SOLIDWORKS PART (.sldprt)
format: sldprt  version: not decoded by parser v0  size: 498,176 bytes
history: native  units: mm
features: extrude x59, sketch x1 (+10 scaffold rows collapsed)
feature tree (70):
  scaffold x10  (default folders/planes/origin — collapsed)
  sketch  "Sketch1"  dims[c1.D1=~12.733394mm c1.D2=~15.484547mm c2.D1=22.86mm c2.D2=2.54mm c2.D4=2.54mm c2.D5=12.7mm c2.D6=2.54mm c2.D7=2.54mm c2.D8=2.54mm c2.D9=2.54mm c2.D10=2.54mm c2.D11=2.54mm c2.D13=10.3124mm c2.D14=~8.032185mm c2.D15=12.7mm c3.D9=2.54mm c3.D19=2.54mm c3.D4=2.54mm c3.D11=2.54mm c3.D18=2.54mm c4.D19=2.54mm c4.D7=~12.249777mm c4.D9=2.54mm c4.D18=2.54mm c5.D9=2.54mm c5.D16=2.54mm c5.D1=19.05mm c5.D2=~75.656875mm c6.D1=~12.696978mm c6.D2=~98.64952mm c7.D1=19.05mm c7.D2=3.175mm c7.D3=10.16mm c8.D2=~9.284402mm c8.D4=~112.960223mm c9.D2=9.525mm c9.D4=~113.490586mm c10.D4=~2.011859deg c11.D4=19.05mm c11.D2=~30.49108deg c12.D2=~13.842804mm c13.D2=~41.841832deg c14.D2=~12.93566mm c14.D12=101.6mm c14.D15=76.2mm c14.D16=~117.088215mm c14.D17=~111.932015mm c15.D16=~117.088215mm c15.D17=9.525mm c16.D16=9.525mm c16.D17=~72.799364mm c16.D15=76.2mm c17.D16=~107.263361mm c17.D17=103.251mm c17.D18=~89.259557mm c18.D18=~179.994237deg c19.D18=16.51mm c19.D19=~12.700868mm c19.D20=12.7mm c19.D21=12.7mm c19.D22=~12.94911mm c19.D23=~7.595379mm c19.D6=7.62mm c19.D10=12.7mm c19.D4=5.08mm c19.D7=15.24mm c19.D8=8.89mm c19.D9=~12.031811mm c20.D9=~30.579227deg c21.D9=~99.101888mm c22.D9=~38.079333deg c23.D9=~12.173949mm]
  extrude  "Extrude6"  Depth=6.35mm RestraintType=0
  extrude  "cosFMVItemName"  [1 undecoded]
  extrude  "cosLBCSymbolColor"  [1 undecoded]
  extrude  "cosRestraintRefPlaneName"  [1 undecoded]
  extrude  "cosFMVItemName"  [1 undecoded]
  extrude  "cosLBCSymbolColor"  [1 undecoded]
  extrude  "cosRestraintRefPlaneName"  [1 undecoded]
  extrude  "cosFMVItemName"  [1 undecoded]
  extrude  "cosLBCSymbolColor"  [1 undecoded]
  extrude  "cosForceRefPlaneName"  [1 undecoded]
  extrude  "cosFMVItemName"  [1 undecoded]
  extrude  "cosDistributionCoordSysName"  [1 undecoded]
  extrude  "cosLBCSymbolColor"  Depth=0 cosForce7=0
  extrude  "cosForceRefPlaneName"  [1 undecoded]
  extrude  "cosFMVItemName"  [1 undecoded]
  extrude  "cosDistributionCoordSysName"  [1 undecoded]
  extrude  "cosLBCSymbolColor"  [1 undecoded]
  extrude  "cosForceRefPlaneName"  [1 undecoded]
  extrude  "cosFMVItemName"  [1 undecoded]
  extrude  "cosDistributionCoordSysName"  [1 undecoded]
  extrude  "cosLBCSymbolColor"  Depth=0 cosFaceID=0
  extrude  "sMaterialSourceName"  [1 undecoded]
  extrude  "sMaterialName"  [1 undecoded]
  extrude  "cosFMVItemName"  [1 undecoded]
  extrude  "cosMaterialName"  [1 undecoded]
  extrude  "cosComponentName"  [1 undecoded]
  extrude  "cosMaterialType"  [1 undecoded]
  extrude  "cosMaterialLibFile"  [1 undecoded]
  extrude  "cosMaterialRefPlaneName"  Depth=0 cosMaterial7=0
  extrude  "sMaterialSourceName"  [1 undecoded]
  extrude  "sMaterialName"  [1 undecoded]
  extrude  "cosFMVItemName"  [1 undecoded]
  extrude  "cosMaterialName"  [1 undecoded]
  extrude  "cosComponentName"  [1 undecoded]
  extrude  "cosMaterialType"  [1 undecoded]
  extrude  "cosMaterialLibFile"  [1 undecoded]
  extrude  "cosMaterialRefPlaneName"  [1 undecoded]
  extrude  "sMaterialSourceName"  [1 undecoded]
  extrude  "sMaterialName"  [1 undecoded]
  extrude  "cosFMVItemName"  [1 undecoded]
  extrude  "cosMaterialName"  [1 undecoded]
  extrude  "cosComponentName"  [1 undecoded]
  extrude  "cosMaterialType"  [1 undecoded]
  extrude  "cosMaterialLibFile"  [1 undecoded]
  extrude  "cosMaterialRefPlaneName"  [1 undecoded]
  extrude  "cosRestraintRefPlaneName"  [1 undecoded]
  extrude  "cosFMVItemName"  [1 undecoded]
  extrude  "cosLBCSymbolColor"  [1 undecoded]
  extrude  "cosRestraintRefPlaneName"  [1 undecoded]
  extrude  "cosFMVItemName"  [1 undecoded]
  extrude  "cosLBCSymbolColor"  [1 undecoded]
  extrude  "cosForceRefPlaneName"  [1 undecoded]
  extrude  "cosFMVItemName"  [1 undecoded]
  extrude  "cosDistributionCoordSysName"  [1 undecoded]
  extrude  "cosLBCSymbolColor"  [1 undecoded]
  extrude  "cosForceRefPlaneName"  [1 undecoded]
  extrude  "cosFMVItemName"  [1 undecoded]
  extrude  "cosDistributionCoordSysName"  [1 undecoded]
  extrude  "cosLBCSymbolColor"  [1 undecoded]
decode coverage: 5 of 60 modeling features carry decoded parameters
note: ~ marks probable driven/reference dimensions
note: 55 parameter values undecoded
summary: no parameter record found for 55 features
note: suppression state not decoded; provenance and decode notes live in map.json
